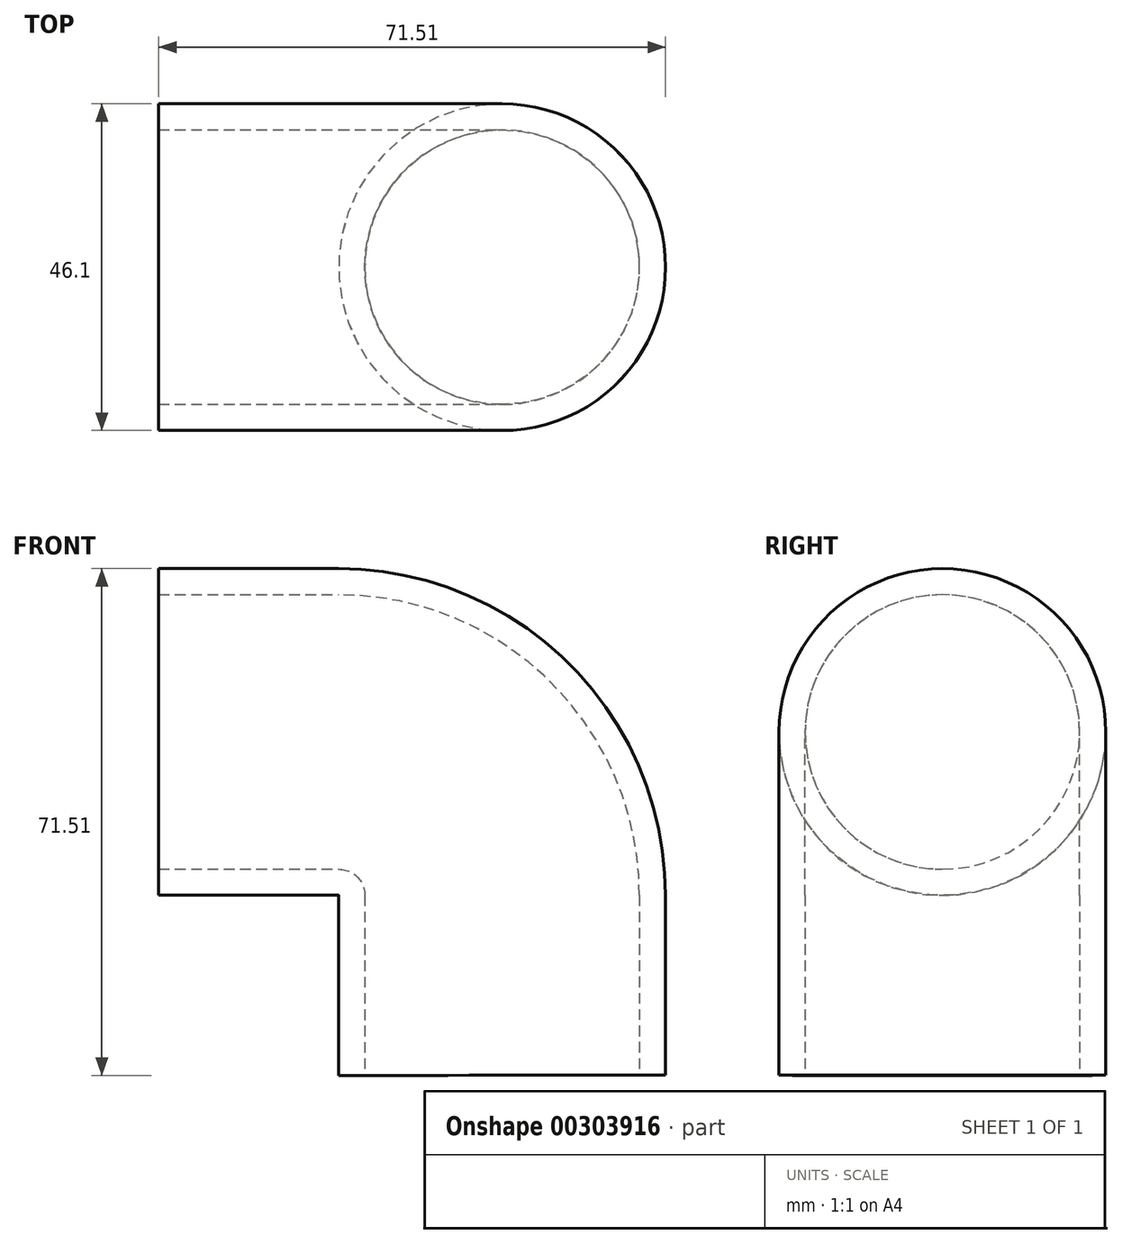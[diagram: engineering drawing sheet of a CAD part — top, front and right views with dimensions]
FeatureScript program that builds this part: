
annotation { "Feature Type Name" : "Feature", "Feature Type Description" : "" }
export const myFeature = defineFeature(function(context is Context, id is Id, definition is map)
    precondition{}
    {
        {
            var Q0;
            Q0=qCreatedBy(makeId("Front.planeOp"),FACE);
            var sketch = newSketch(context, id + "F0", { "sketchPlane" : qUnion([Q0])});
            skLineSegment(sketch, "E0", {"start": v(0, 0) * mm, "end": v(-25.4, 0) * mm});
            skLineSegment(sketch, "E1", {"start": v(-25.4, -23.05) * mm, "end": v(-25.4, 0) * mm});
            skLineSegment(sketch, "E2", {"start": v(-25.4, 0) * mm, "end": v(-25.4, 23.05) * mm});
            skLineSegment(sketch, "E3", {"start": v(0, 0) * mm, "end": v(0, -48.45) * mm, "construction": true});
            skLineSegment(sketch, "E4", {"start": v(0, -48.45) * mm, "end": v(23.06, -48.45) * mm, "construction": true});
            skLineSegment(sketch, "E5", {"start": v(-25.4, 23.05) * mm, "end": v(0, 23.05) * mm, "construction": true});
            skLineSegment(sketch, "E6", {"start": v(0, 23.05) * mm, "end": v(0, -23.05) * mm, "construction": true});
            skLineSegment(sketch, "E7", {"start": v(0, -23.05) * mm, "end": v(-25.4, -23.05) * mm, "construction": true});
            skLineSegment(sketch, "E8", {"start": v(0, -23.05) * mm, "end": v(46.1, -23.05) * mm, "construction": true});
            skLineSegment(sketch, "E9", {"start": v(46.1, -23.05) * mm, "end": v(46.1, -48.45) * mm, "construction": true});
            skLineSegment(sketch, "E10", {"start": v(46.1, -48.45) * mm, "end": v(23.06, -48.45) * mm});
            skLineSegment(sketch, "E11", {"start": v(23.06, -48.45) * mm, "end": v(23.05, -23.05) * mm});
            skArc(sketch, "E12", {"start": v(23.05, -23.05) * mm, "mid": v(16.3, -6.75) * mm, "end": v(0, 0) * mm});
            skSolve(sketch);
        }
        {
            var Q0;
            Q0=sQuery(id+"F0.wireOp",EDGE,"E2");
            var Q1;
            Q1=sQuery(id+"F0.wireOp",EDGE,"E0");
            revolve(context, id + "F1", {"bodyType" : ToolBodyType.SURFACE, "surfaceEntities" : qUnion([Q0]), "axis" : qUnion([Q1]), "revolveType" : RevolveType.FULL});
        }
        {
            var Q0;
            Q0=makeQuery(id+"F1.opRevolve","SWEPT_FACE",FACE,{"disambiguationData":[OSD([sQuery(id+"F0.wireOp",EDGE,"E2")])]});
            var Q1;
            Q1=sQuery(id+"F0.wireOp",EDGE,"E0");
            var Q2;
            Q2=sQuery(id+"F0.wireOp",EDGE,"E12");
            var Q3;
            Q3=sQuery(id+"F0.wireOp",EDGE,"E11");
            sweep(context, id + "F2", {"profiles" : qUnion([Q0]), "path" : qUnion([Q1, Q2, Q3])});
        }
        {
            var Q0;
            Q0=makeQuery(id+"F2.opSweep","CAP_FACE",FACE,{"disambiguationData":[OSD([sQuery(id+"F0.wireOp",VERTEX,"E11.start"),sQuery(id+"F0.wireOp",EDGE,"E2")])],"isStart":false});
            var Q1;
            Q1=makeQuery(id+"F2.opSweep","CAP_FACE",FACE,{"disambiguationData":[OSD([sQuery(id+"F0.wireOp",VERTEX,"E0.end"),sQuery(id+"F0.wireOp",EDGE,"E2")])],"isStart":true});
            shell(context, id + "F3", {"entities" : qUnion([Q0, Q1]), "thickness" : 3.68 * mm});
        }
    });
